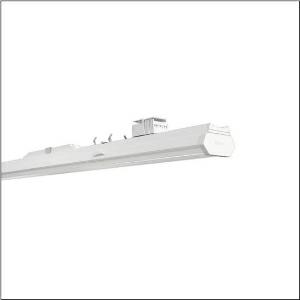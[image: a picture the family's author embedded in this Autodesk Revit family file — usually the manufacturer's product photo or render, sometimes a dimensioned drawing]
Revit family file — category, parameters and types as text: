
# Revit family: licross_r__11_protected_mo_51tp117n485g_c591
name_source: partatom
category: Lighting Fixtures
units: mm (PartAtom-declared; Revit-internal decimal feet)

## family parameters
Cut with Voids When Loaded = No
Host = Face
Light Source = No
Part Type = Normal
Room Calculation Point = No
Round Connector Dimension = Use Diameter
Shared = No

## types (1)
- Licross® 11 Protected MO (1 x LED, 8680 lm, 48.6 W, 4000K)
    Apparent Load = 49 VA
    CIE Flux Codes = 83 94 98 100 100
    Color Rendering = 80
    Color Temperature = 4000K
    Default Elevation = 1800 mm
    Description = Licross® 11 Protected MO, luminaire insert, of sheet steel, galvanised, coil coated, white, length: 1.500mm, width: 90mm, height: 101mm, LED rated luminous flux: 8.680lm, light colour: 840, control gear: ON/OFF, with plug, 3-pole, with phase selection, mains connection: 220..240V, AC, 50/60Hz, rated input power: 49W, halogen-free wiring, primary light control with lens, of plastic, primary optical cover: cover, of PMMA, light emission: direct distribution, primary light characteristic: symmetric, protection rating (complete): IP64, insulation class (complete): insulation class I (protective earthing), certification: CE, ENEC, VDE, UKCA, protection symbol: D if used in an environment with conductive dust loads with corresponding accessories, impact resistance: IK06, permissible ambient temperature for indoor applications: -25..+35°C, corresponds to IFS (International Featured Standards) requirements for safety and quality in the food industry, reducing of maximum allowable ambient temperature of 5°C with ceiling mounting, LABS conformity tested according to VDMA 24364:2018-05, packaging unit: 1 piece
    Height = 92 mm
    Lamp = 1 x LED
    Lamp Light Flux = 8680 lm
    Lamp Power = 48.6 W
    Lamp count = 1
    Length = 1500 mm
    Luminous efficacy = 179 lm/W
    Manufacturer = Siteco
    ModVariant = No
    Model = 51TP117N485G
    Mounting Place = Ceiling
    Mounting Type = Pendant
    Number of Poles = 1
    OnlyDefault = Yes
    Power Factor = 1
    Product Name = Licross® 11 Protected MO
    Product group = luminaire insert
    ProductGroupID = 902
    Protection Class = Protection class I
    Protection Degree = IP 64
    RLX_Detail_Level = 1
    RLX_Emergency_Light_Flux = 0 lm
    RLX_Emergency_Type = 0
    RLX_Emergency_Type_DB = No
    RlxData = <blob elided: 20353 chars, md5=2fe9ee9a>
    Socket = socket
    Standby Power = 0 W
    System Light Flux = 8680 lm
    System Power = 49 W
    Type Comments = Product without accessories
    Type Image = l_1256148.jpg
    URL = http://relux.com
    VarID = ---
    Voltage = 0 V
    Weight = 0.00 kg
    Width = 88 mm

## geometry (parser evidence)
native form markers: Blend x4, Sweep x11
no freeform markers — native parametric forms only
